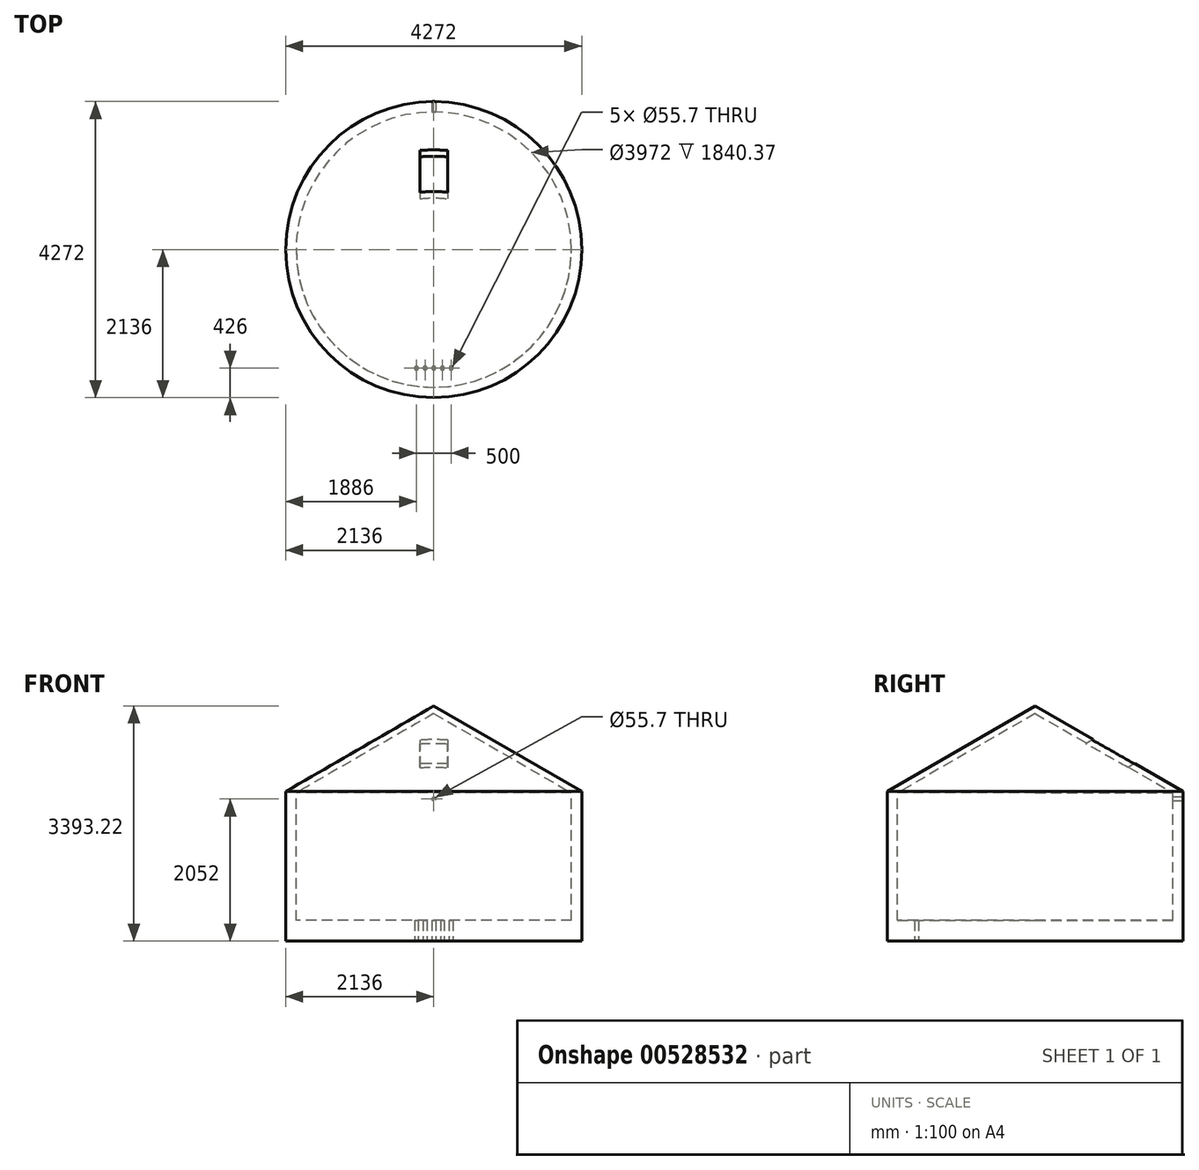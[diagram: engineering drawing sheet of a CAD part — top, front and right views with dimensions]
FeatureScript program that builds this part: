
annotation { "Feature Type Name" : "Feature", "Feature Type Description" : "" }
export const myFeature = defineFeature(function(context is Context, id is Id, definition is map)
    precondition{}
    {
        {
            var Q0;
            Q0=qCreatedBy(makeId("Front.planeOp"),FACE);
            var sketch = newSketch(context, id + "F0", { "sketchPlane" : qUnion([Q0])});
            skLineSegment(sketch, "E0", {"start": v(0, 0) * mm, "end": v(2136, 0) * mm});
            skLineSegment(sketch, "E1", {"start": v(2136, 0) * mm, "end": v(2136, 2160) * mm});
            skLineSegment(sketch, "E2", {"start": v(2136, 2160) * mm, "end": v(0, 3393.22) * mm});
            skLineSegment(sketch, "E3", {"start": v(0, 3393.22) * mm, "end": v(0, 3286.99) * mm});
            skLineSegment(sketch, "E4", {"start": v(0, 3286.99) * mm, "end": v(1986, 2140.37) * mm});
            skLineSegment(sketch, "E5", {"start": v(1986, 2140.37) * mm, "end": v(1986, 300) * mm});
            skLineSegment(sketch, "E6", {"start": v(1986, 300) * mm, "end": v(0, 300) * mm});
            skLineSegment(sketch, "E7", {"start": v(0, 300) * mm, "end": v(0, 0) * mm});
            skSolve(sketch);
        }
        {
            var Q0;
            Q0=sQuery(id+"F0.wireOp",EDGE,"E0");
            cPlane(context, id + "F1", {"entities" : qUnion([Q0]), "cplaneType" : CPlaneType.LINE_ANGLE, "offset" : 25 * mm, "angle" : 30 * degree, "width" : 150 * mm, "height" : 150 * mm});
        }
        {
            var Q0;
            Q0=qCreatedBy(id+"F1.planeOp",FACE);
            var sketch = newSketch(context, id + "F2", { "sketchPlane" : qUnion([Q0])});
            skLineSegment(sketch, "E8.bottom", {"start": v(-200, 2100) * mm, "end": v(200, 2100) * mm});
            skLineSegment(sketch, "E8.top", {"start": v(-200, 1500) * mm, "end": v(200, 1500) * mm});
            skLineSegment(sketch, "E8.left", {"start": v(-200, 2100) * mm, "end": v(-200, 1500) * mm});
            skLineSegment(sketch, "E9.MirrorCS", {"start": v(200, 2100) * mm, "end": v(200, 1500) * mm});
            skSolve(sketch);
        }
        {
            var Q0;
            Q0=qCreatedBy(makeId("Top.planeOp"),FACE);
            var sketch = newSketch(context, id + "F3", { "sketchPlane" : qUnion([Q0])});
            skLineSegment(sketch, "E10", {"start": v(282.73, -1710) * mm, "end": v(-1173.43, -1710) * mm, "construction": true});
            skCircle(sketch, "E11", {"center": v(125, -1710) * mm, "radius": 27.85 * mm});
            skCircle(sketch, "E12", {"center": v(-250, -1710) * mm, "radius": 27.85 * mm});
            skCircle(sketch, "E13", {"center": v(-125, -1710) * mm, "radius": 27.85 * mm});
            skCircle(sketch, "E14", {"center": v(0, -1710) * mm, "radius": 27.85 * mm});
            skCircle(sketch, "E15", {"center": v(250, -1710) * mm, "radius": 27.85 * mm});
            skSolve(sketch);
        }
        {
            var Q0;
            Q0=makeQuery(id+"F0.imprint","IMPRINT",FACE,{"disambiguationData":[TD([[makeQuery(id+"F0.imprint","IMPRINT",EDGE,{"derivedFrom":sQuery(id+"F0.wireOp",EDGE,"E0")}),1.0]])]});
            var Q1;
            Q1=sQuery(id+"F0.wireOp",EDGE,"E7");
            revolve(context, id + "F4", {"entities" : qUnion([Q0]), "axis" : qUnion([Q1]), "revolveType" : RevolveType.FULL});
        }
        {
            var Q0;
            Q0=makeQuery(id+"F2.imprint","IMPRINT",FACE,{"disambiguationData":[TD([[makeQuery(id+"F2.imprint","IMPRINT",EDGE,{"derivedFrom":sQuery(id+"F2.wireOp",EDGE,"E8.bottom")}),-1.0]])]});
            extrude(context, id + "F5", {"entities" : qUnion([Q0]), "operationType" : NewBodyOperationType.REMOVE, "depth" : 30000 * mm, "offsetDistance" : 25 * mm});
        }
        {
            var Q0;
            Q0=makeQuery(id+"F3.imprint","IMPRINT",FACE,{"disambiguationData":[TD([[makeQuery(id+"F3.imprint","IMPRINT",EDGE,{"derivedFrom":sQuery(id+"F3.wireOp",EDGE,"E11")}),1.0]])]});
            var Q1;
            Q1=makeQuery(id+"F3.imprint","IMPRINT",FACE,{"disambiguationData":[TD([[makeQuery(id+"F3.imprint","IMPRINT",EDGE,{"derivedFrom":sQuery(id+"F3.wireOp",EDGE,"E14")}),1.0]])]});
            var Q2;
            Q2=makeQuery(id+"F3.imprint","IMPRINT",FACE,{"disambiguationData":[TD([[makeQuery(id+"F3.imprint","IMPRINT",EDGE,{"derivedFrom":sQuery(id+"F3.wireOp",EDGE,"E13")}),1.0]])]});
            var Q3;
            Q3=makeQuery(id+"F3.imprint","IMPRINT",FACE,{"disambiguationData":[TD([[makeQuery(id+"F3.imprint","IMPRINT",EDGE,{"derivedFrom":sQuery(id+"F3.wireOp",EDGE,"E12")}),1.0]])]});
            var Q4;
            Q4=makeQuery(id+"F3.imprint","IMPRINT",FACE,{"disambiguationData":[TD([[makeQuery(id+"F3.imprint","IMPRINT",EDGE,{"derivedFrom":sQuery(id+"F3.wireOp",EDGE,"E15")}),1.0]])]});
            extrude(context, id + "F6", {"entities" : qUnion([Q0, Q1, Q2, Q3, Q4]), "operationType" : NewBodyOperationType.REMOVE, "depth" : 500 * mm, "offsetDistance" : 25 * mm});
        }
        {
            var Q0;
            Q0=qCreatedBy(makeId("Front.planeOp"),FACE);
            var sketch = newSketch(context, id + "F7", { "sketchPlane" : qUnion([Q0])});
            skCircle(sketch, "E16", {"center": v(0, 2052) * mm, "radius": 27.85 * mm});
            skSolve(sketch);
        }
        {
            var Q0;
            Q0=qSketchRegion(id+"F7",true);
            extrude(context, id + "F8", {"entities" : qUnion([Q0]), "operationType" : NewBodyOperationType.REMOVE, "endBound" : BoundingType.THROUGH_ALL, "oppositeDirection" : true, "depth" : 25 * mm, "offsetDistance" : 25 * mm});
        }
    });
